# Revit family: Workstations-Height_Adjustable-Teknion-BHKFH-Mid_Height_Fixed_Run_Off-R2018
name_source: partatom
category: Furniture
revit_build: Autodesk Revit 2018 (Build: 20190510_1515(x64)
units: mm (PartAtom-declared; Revit-internal decimal feet)

## family parameters
Always vertical = Yes
Cut with Voids When Loaded = No
OmniClass Number = 23.40.20.00
OmniClass Title = General Furniture and Specialties
Room Calculation Point = No
Shared = Yes
Work Plane-Based = No

## types (5) — shared parameters
Assembly Code = E2020200
Manufacturer = Teknion
Manufacturer Fax = 416.661.4586
Part Number = BHKFH
Product Documentation Link = https://www.teknion.com
Product Line = Expansion Casegoods
Product Page URL = https://www.teknion.com
Series = Expansion Casegoods
Sustainability Data = https://www.teknion.com
URL = www.teknion.com
Unit Weight URL = http://www.teknion.com
Warranty = http://www.teknion.com

## per-type parameters (varying)
| type | Actual Width | Description | Model | Width |
| 66" Width | 65.67 " | Mid-Height Kneespace Module Height-Adjustability and Fixed Run-Off, 9" Depth, 66" Width, 21" Height | BHKFH96621_ | 66 " |
| 72" Width | 71.64 " | Mid-Height Kneespace Module Height-Adjustability and Fixed Run-Off, 9" Depth, 72" Width, 21" Height | BHKFH97221_ | 72 " |
| 78" Width | 77.61 " | Mid-Height Kneespace Module Height-Adjustability and Fixed Run-Off, 9" Depth, 78" Width, 21" Height | BHKFH97821_ | 78 " |
| 84" Width | 83.58 " | Mid-Height Kneespace Module Height-Adjustability and Fixed Run-Off, 9" Depth, 84" Width, 21" Height | BHKFH98421_ | 84 " |
| 90" Width | 89.55 " | Mid-Height Kneespace Module Height-Adjustability and Fixed Run-Off, 9" Depth, 90" Width, 21" Height | BHKFH99021_ | 90 " |

## geometry (parser evidence)
native form markers: Sweep x2
no freeform markers — native parametric forms only
